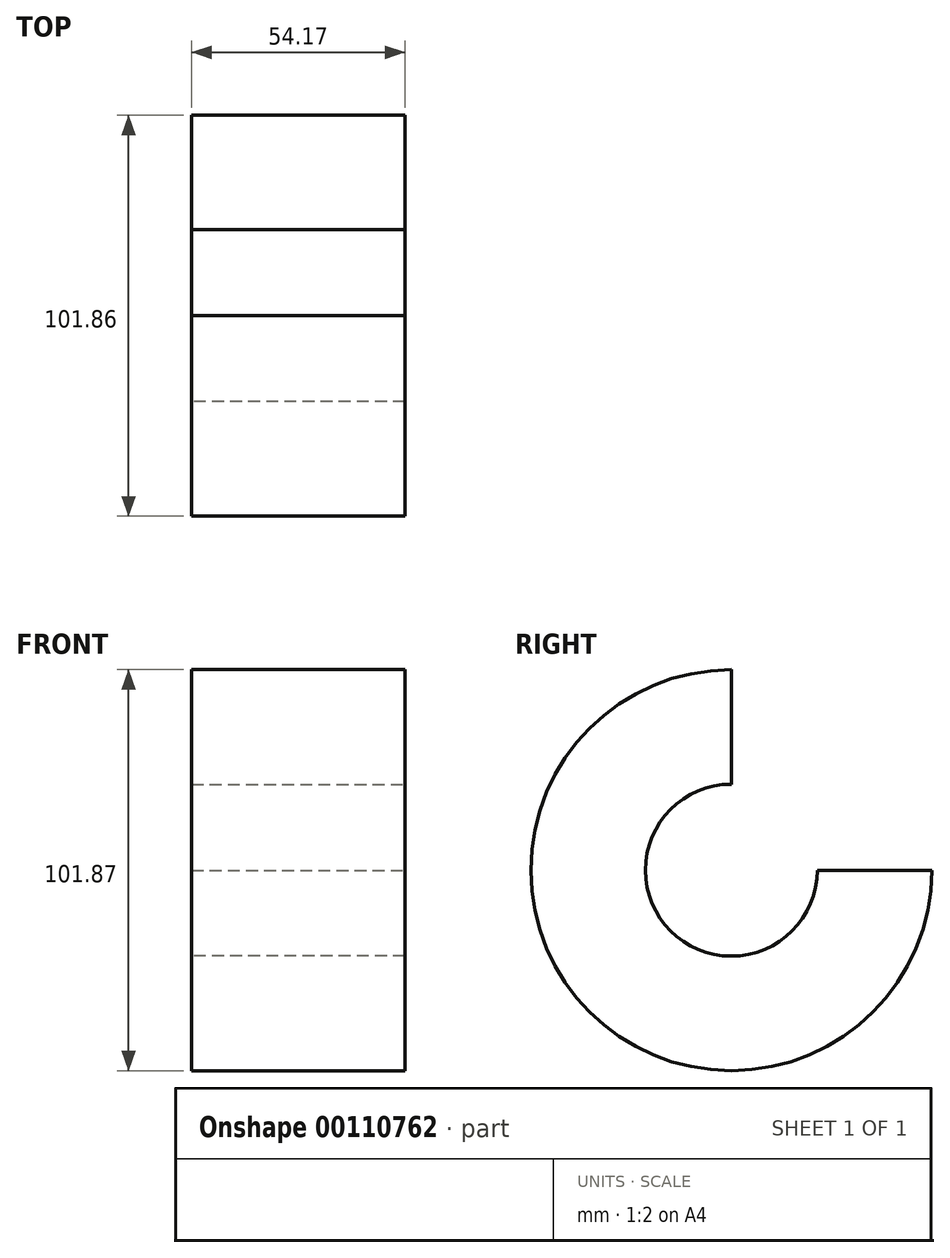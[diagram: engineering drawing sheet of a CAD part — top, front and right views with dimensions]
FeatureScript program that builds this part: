
annotation { "Feature Type Name" : "Feature", "Feature Type Description" : "" }
export const myFeature = defineFeature(function(context is Context, id is Id, definition is map)
    precondition{}
    {
        {
            var Q0;
            Q0=qCreatedBy(makeId("Front.planeOp"),FACE);
            var sketch = newSketch(context, id + "F0", { "sketchPlane" : qUnion([Q0])});
            skLineSegment(sketch, "E0", {"start": v(-34.76, 6.84) * mm, "end": v(31.54, 6.84) * mm});
            skLineSegment(sketch, "E1.bottom", {"start": v(-25.87, 57.77) * mm, "end": v(28.3, 57.77) * mm});
            skLineSegment(sketch, "E1.top", {"start": v(-25.87, 28.66) * mm, "end": v(28.3, 28.66) * mm});
            skLineSegment(sketch, "E1.left", {"start": v(-25.87, 57.77) * mm, "end": v(-25.87, 28.66) * mm});
            skLineSegment(sketch, "E1.right", {"start": v(28.3, 57.77) * mm, "end": v(28.3, 28.66) * mm});
            skSolve(sketch);
        }
        {
            var Q0;
            Q0=makeQuery(id+"F0.imprint","IMPRINT",FACE,{"disambiguationData":[TD([[makeQuery(id+"F0.imprint","IMPRINT",EDGE,{"derivedFrom":sQuery(id+"F0.wireOp",EDGE,"E1.bottom")}),-1.0]])]});
            var Q1;
            Q1=sQuery(id+"F0.wireOp",EDGE,"E0");
            revolve(context, id + "F1", {"entities" : qUnion([Q0]), "axis" : qUnion([Q1]), "revolveType" : RevolveType.ONE_DIRECTION, "angle" : 270 * degree});
        }
    });
